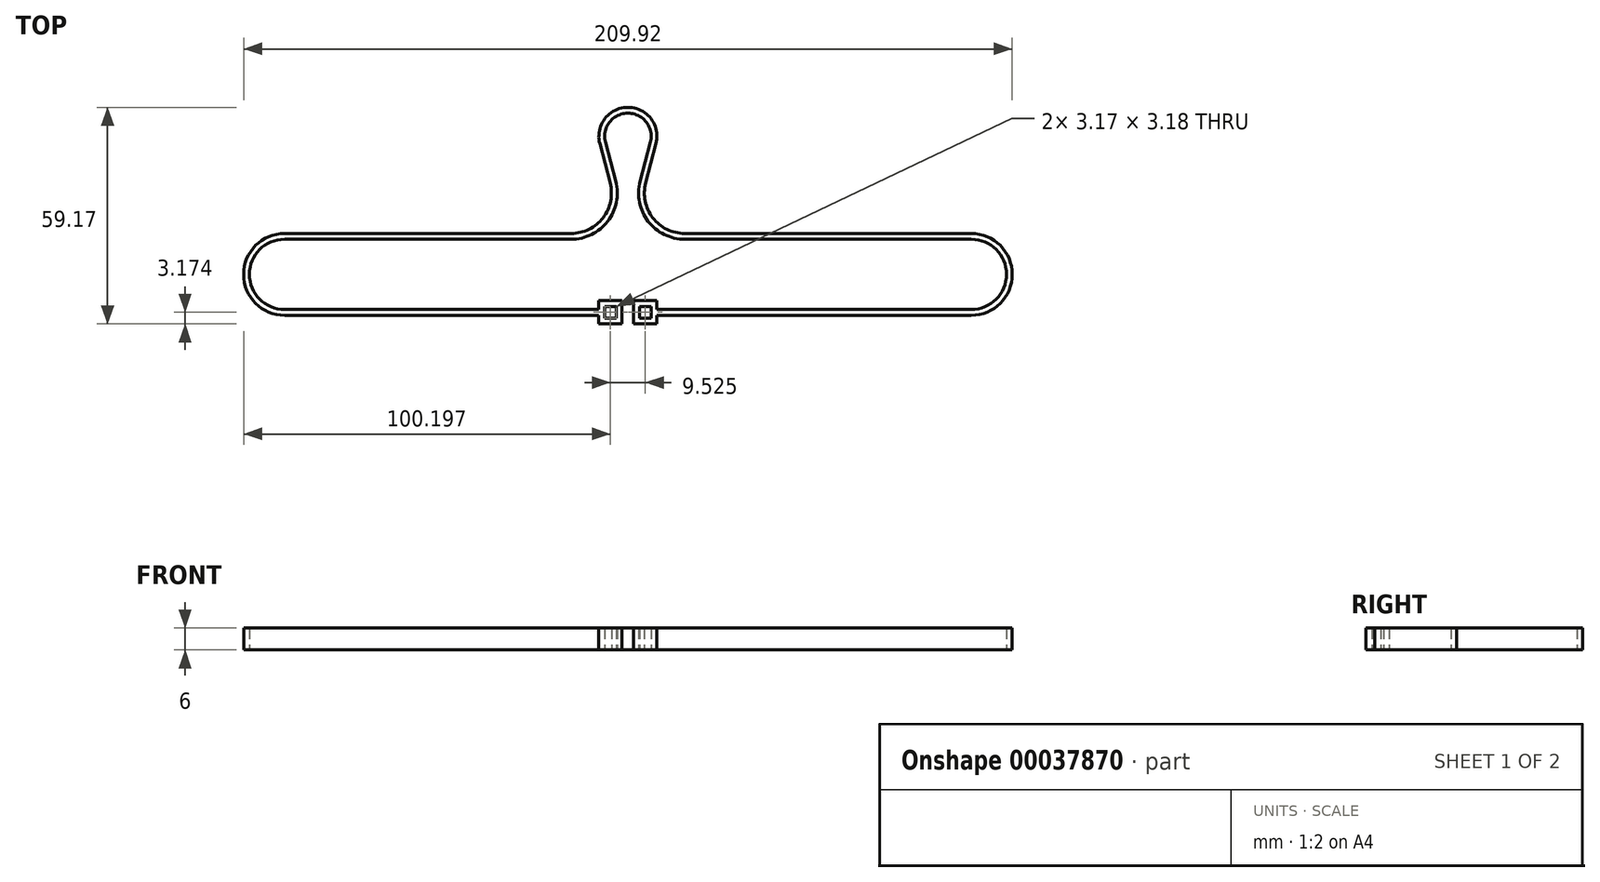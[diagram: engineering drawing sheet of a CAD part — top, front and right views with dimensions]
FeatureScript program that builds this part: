
annotation { "Feature Type Name" : "Feature", "Feature Type Description" : "" }
export const myFeature = defineFeature(function(context is Context, id is Id, definition is map)
    precondition{}
    {
        {
            var Q0;
            Q0=qCreatedBy(makeId("Top.planeOp"),FACE);
            var sketch = newSketch(context, id + "F0", { "sketchPlane" : qUnion([Q0])});
            skArc(sketch, "E0", {"start": v(6.14, -1.62) * mm, "mid": v(0, 6.35) * mm, "end": v(-6.14, -1.62) * mm});
            skLineSegment(sketch, "E1", {"start": v(0, 0) * mm, "end": v(0, -15.5) * mm, "construction": true});
            skLineSegment(sketch, "E2", {"start": v(-15.5, -15.5) * mm, "end": v(15.5, -15.5) * mm, "construction": true});
            skArc(sketch, "E3", {"start": v(-15.5, -26.5) * mm, "mid": v(-6.79, -22.21) * mm, "end": v(-4.86, -12.7) * mm});
            skArc(sketch, "E4", {"start": v(4.86, -12.7) * mm, "mid": v(6.79, -22.21) * mm, "end": v(15.5, -26.5) * mm});
            skLineSegment(sketch, "E5", {"start": v(-4.86, -12.7) * mm, "end": v(-7.68, -2.02) * mm});
            skLineSegment(sketch, "E6", {"start": v(4.86, -12.7) * mm, "end": v(7.68, -2.02) * mm});
            skArc(sketch, "E7", {"start": v(3.33, -12.3) * mm, "mid": v(5.53, -23.18) * mm, "end": v(15.5, -28.09) * mm});
            skArc(sketch, "E8", {"start": v(-15.5, -28.09) * mm, "mid": v(-5.53, -23.18) * mm, "end": v(-3.33, -12.3) * mm});
            skLineSegment(sketch, "E9", {"start": v(15.5, -26.5) * mm, "end": v(15.5, -28.09) * mm, "construction": true});
            skLineSegment(sketch, "E10", {"start": v(-15.5, -26.5) * mm, "end": v(-15.5, -28.09) * mm, "construction": true});
            skLineSegment(sketch, "E11", {"start": v(15.5, -15.5) * mm, "end": v(15.5, -26.5) * mm, "construction": true});
            skLineSegment(sketch, "E12", {"start": v(-15.5, -15.5) * mm, "end": v(-15.5, -26.5) * mm, "construction": true});
            skLineSegment(sketch, "E13", {"start": v(6.14, -1.62) * mm, "end": v(3.33, -12.3) * mm});
            skArc(sketch, "E14", {"start": v(7.68, -2.02) * mm, "mid": v(0, 7.94) * mm, "end": v(-7.68, -2.02) * mm});
            skLineSegment(sketch, "E15", {"start": v(-6.14, -1.62) * mm, "end": v(-3.33, -12.3) * mm});
            skLineSegment(sketch, "E16", {"start": v(-15.5, -26.5) * mm, "end": v(-93.79, -26.5) * mm});
            skLineSegment(sketch, "E17", {"start": v(-15.5, -28.09) * mm, "end": v(-93.79, -28.09) * mm});
            skLineSegment(sketch, "E18", {"start": v(15.5, -28.09) * mm, "end": v(93.79, -28.09) * mm});
            skLineSegment(sketch, "E19", {"start": v(15.5, -26.5) * mm, "end": v(93.79, -26.5) * mm});
            skLineSegment(sketch, "E20", {"start": v(-93.79, -28.09) * mm, "end": v(-93.79, -47.26) * mm, "construction": true});
            skLineSegment(sketch, "E21", {"start": v(93.79, -28.09) * mm, "end": v(93.79, -47.26) * mm, "construction": true});
            skArc(sketch, "E22", {"start": v(-93.79, -28.09) * mm, "mid": v(-103.38, -37.67) * mm, "end": v(-93.79, -47.26) * mm});
            skArc(sketch, "E23", {"start": v(-93.79, -26.5) * mm, "mid": v(-104.96, -37.67) * mm, "end": v(-93.79, -48.85) * mm});
            skLineSegment(sketch, "E24", {"start": v(-93.79, -47.26) * mm, "end": v(-7.94, -47.26) * mm});
            skLineSegment(sketch, "E25", {"start": v(-7.94, -47.26) * mm, "end": v(-7.94, -44.88) * mm});
            skLineSegment(sketch, "E26", {"start": v(-7.94, -44.88) * mm, "end": v(-1.59, -44.88) * mm});
            skLineSegment(sketch, "E27", {"start": v(-1.59, -44.88) * mm, "end": v(-1.59, -51.23) * mm});
            skLineSegment(sketch, "E28", {"start": v(-93.79, -48.85) * mm, "end": v(-7.94, -48.85) * mm});
            skLineSegment(sketch, "E29.bottom", {"start": v(-6.35, -49.64) * mm, "end": v(-3.18, -49.64) * mm});
            skLineSegment(sketch, "E29.top", {"start": v(-6.35, -46.47) * mm, "end": v(-3.18, -46.47) * mm});
            skLineSegment(sketch, "E29.left", {"start": v(-6.35, -49.64) * mm, "end": v(-6.35, -46.47) * mm});
            skLineSegment(sketch, "E29.right", {"start": v(-3.18, -49.64) * mm, "end": v(-3.18, -46.47) * mm});
            skLineSegment(sketch, "E30", {"start": v(-4.76, -46.47) * mm, "end": v(-4.76, -44.88) * mm, "construction": true});
            skArc(sketch, "E31", {"start": v(93.79, -47.26) * mm, "mid": v(103.38, -37.67) * mm, "end": v(93.79, -28.09) * mm});
            skArc(sketch, "E32", {"start": v(93.79, -48.85) * mm, "mid": v(104.96, -37.67) * mm, "end": v(93.79, -26.5) * mm});
            skLineSegment(sketch, "E33", {"start": v(93.79, -47.26) * mm, "end": v(7.94, -47.26) * mm});
            skLineSegment(sketch, "E34", {"start": v(93.79, -48.85) * mm, "end": v(7.94, -48.85) * mm});
            skLineSegment(sketch, "E35.bottom", {"start": v(3.18, -46.47) * mm, "end": v(6.35, -46.47) * mm});
            skLineSegment(sketch, "E35.top", {"start": v(3.17, -49.64) * mm, "end": v(6.35, -49.64) * mm});
            skLineSegment(sketch, "E35.left", {"start": v(3.17, -46.47) * mm, "end": v(3.17, -49.64) * mm});
            skLineSegment(sketch, "E35.right", {"start": v(6.35, -46.47) * mm, "end": v(6.35, -49.64) * mm});
            skLineSegment(sketch, "E36", {"start": v(4.76, -46.47) * mm, "end": v(4.76, -44.88) * mm});
            skLineSegment(sketch, "E37", {"start": v(1.59, -51.23) * mm, "end": v(1.59, -44.88) * mm});
            skLineSegment(sketch, "E38", {"start": v(1.59, -44.88) * mm, "end": v(7.94, -44.88) * mm});
            skLineSegment(sketch, "E39", {"start": v(7.94, -44.88) * mm, "end": v(7.94, -47.26) * mm});
            skLineSegment(sketch, "E40", {"start": v(-3.18, -48.06) * mm, "end": v(-1.59, -48.06) * mm, "construction": true});
            skPoint(sketch, "E40.endSnap0", {"position": v(-3.18, -48.06) * mm});
            skLineSegment(sketch, "E41", {"start": v(3.17, -48.06) * mm, "end": v(1.59, -48.06) * mm, "construction": true});
            skPoint(sketch, "E41.endSnap0", {"position": v(3.17, -48.06) * mm});
            skLineSegment(sketch, "E42", {"start": v(-1.59, -51.23) * mm, "end": v(-7.94, -51.23) * mm});
            skLineSegment(sketch, "E43", {"start": v(-7.94, -51.23) * mm, "end": v(-7.94, -48.85) * mm});
            skLineSegment(sketch, "E44", {"start": v(1.59, -51.23) * mm, "end": v(7.94, -51.23) * mm});
            skLineSegment(sketch, "E45", {"start": v(7.94, -51.23) * mm, "end": v(7.94, -48.85) * mm});
            skSolve(sketch);
        }
        {
            var Q0;
            Q0 = qSketchRegion(id + "F0", true);
            extrude(context, id + "F1", {"entities" : qUnion([Q0]), "depth" : 6 * mm});
        }
    });
